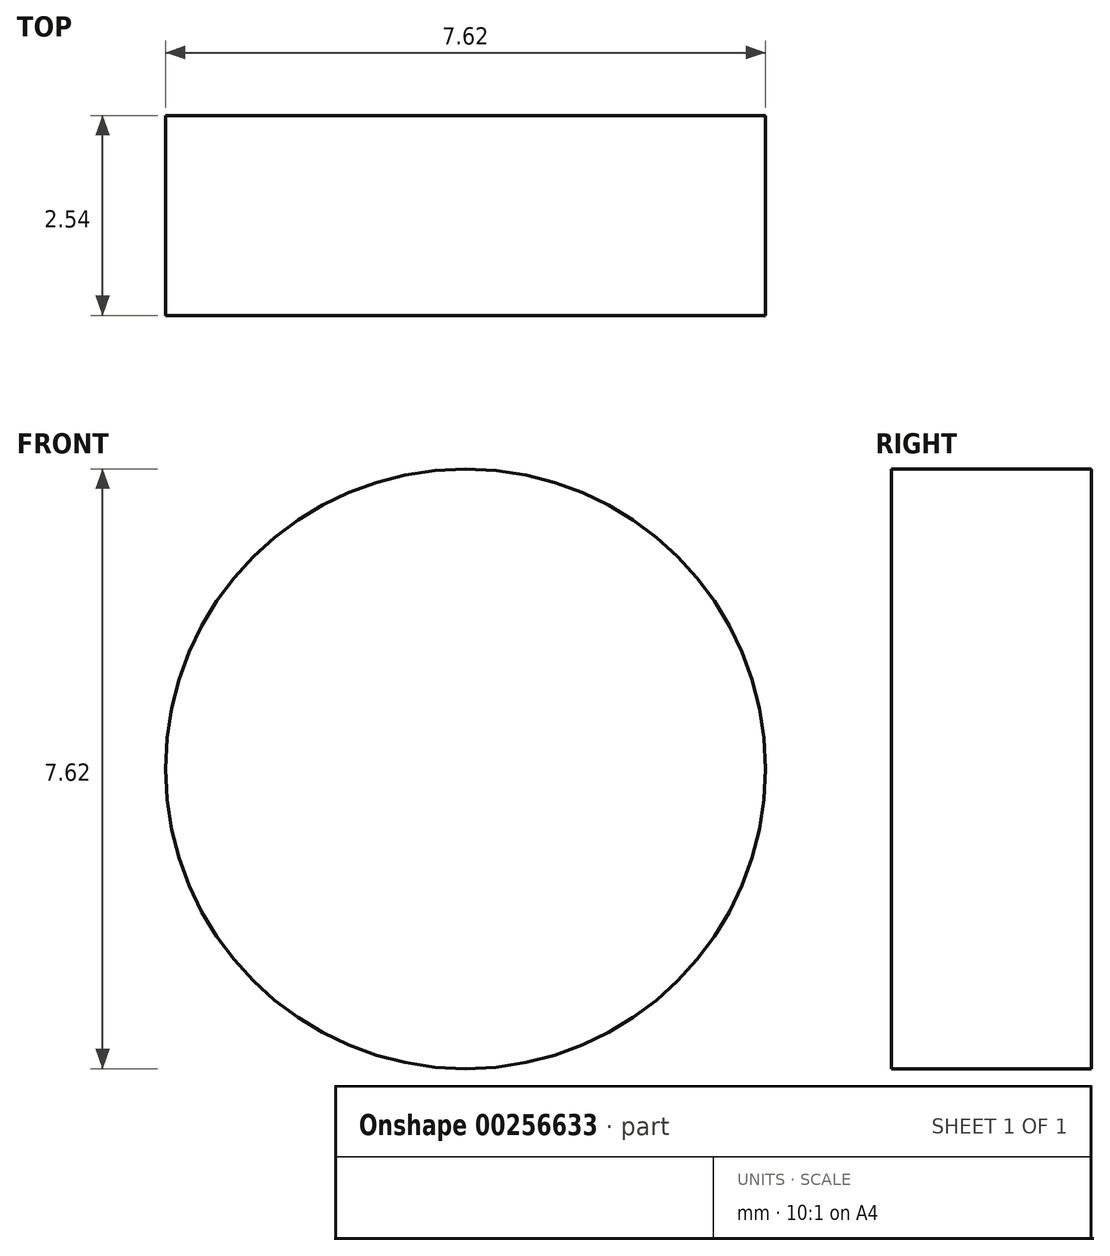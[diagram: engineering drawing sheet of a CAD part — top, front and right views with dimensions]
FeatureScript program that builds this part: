
annotation { "Feature Type Name" : "Feature", "Feature Type Description" : "" }
export const myFeature = defineFeature(function(context is Context, id is Id, definition is map)
    precondition{}
    {
        {
            var Q0;
            Q0=qCreatedBy(makeId("Front.planeOp"),FACE);
            var sketch = newSketch(context, id + "F0", { "sketchPlane" : qUnion([Q0])});
            skCircle(sketch, "E0", {"center": v(0, 0) * mm, "radius": 3.8 * mm});
            skSolve(sketch);
        }
        {
            var Q0;
            Q0=makeQuery(id+"F0.imprint","IMPRINT",FACE,{"disambiguationData":[TD([[makeQuery(id+"F0.imprint","IMPRINT",EDGE,{"derivedFrom":sQuery(id+"F0.wireOp",EDGE,"E0")}),1.0]])]});
            extrude(context, id + "F1", {"entities" : qUnion([Q0]), "depth" : 2.54 * mm});
        }
    });
